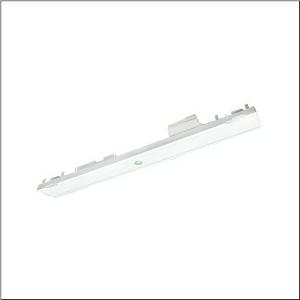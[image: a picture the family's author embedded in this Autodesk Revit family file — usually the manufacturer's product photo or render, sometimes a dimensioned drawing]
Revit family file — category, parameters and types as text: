
# Revit family: licross_56tl117c4x31
name_source: partatom
category: Lighting Fixtures
units: mm (PartAtom-declared; Revit-internal decimal feet)

## family parameters
Cut with Voids When Loaded = No
Host = Face
Light Source = No
Part Type = Normal
Room Calculation Point = No
Round Connector Dimension = Use Diameter
Shared = No

## types (1)
- Licross (1 x LED, 310 lm, 3.9 W, 4000K)
    Apparent Load = 4 VA
    CIE Flux Codes = 84 95 98 100 100
    Color Rendering = 70
    Color Temperature = 4000K
    Default Elevation = 1800 mm
    Description = Licross, luminaire insert, of sheet steel, coil coated, white, length: 500mm, width: 59mm, height: 60mm, mounting height: 7..17m, emergency light element,LED rated luminous flux: 310lm, light colour: 740, control gear: CEAG, with plug, 6-pole, with phase selection, mains connection: 220..240V, AC/DC, 0/50..60Hz, rated input power: 3.9W, internal wiring halogen-free, for trunking rail, 9..14-core, for emergency light function, supply monitoring module CEAG, with address switch, choice between two emergency light lines via tool-free moving of contact pin prior to installation in trunking rail, primary light control with lens, of PMMA, primary optical cover: cover, of PMMA, light emission: direct distribution, primary light characteristic: symmetric,  for area, compatible with all CEAG STAR technology systems (ZB-S, DG-S (DualGuard-S), LP-STAR, AT-S+), protection rating (complete): IP40, insulation class (complete): insulation class I (protective earthing), certification: CE, UKCA, protection symbol: D if used in an environment without relevant dust loads, impact resistance: IK06, permissible ambient temperature for indoor applications: -20..+40°C, packaging unit: 1 piece
    Height = 60 mm  [stored 0.19685 ft]
    Lamp = 1 x LED
    Lamp Light Flux = 310 lm
    Lamp Power = 3.9 W
    Lamp count = 1
    Length = 500 mm  [stored 1.64042 ft]
    Luminous efficacy = 79 lm/W
    Manufacturer = Siteco
    ModVariant = No
    Model = 56TL117C4X31
    Mounting Place = Ceiling
    Mounting Type = Pendant
    Number of Poles = 1
    OnlyDefault = Yes
    Power Factor = 1
    Product Name = Licross
    Product group = luminaire insert | ceiling pendant
    ProductGroupID = 901
    Protection Class = Protection class I
    Protection Degree = IP 40
    RLX_Detail_Level = 1
    RLX_Emergency_Light_Flux = 0 lm
    RLX_Emergency_Type = 0
    RLX_Emergency_Type_DB = No
    RlxData = <blob elided: 17845 chars, md5=55b05414>
    Socket = socket
    Standby Power = 0 W
    System Light Flux = 310 lm
    System Power = 4 W
    Type Comments = Product without accessories
    Type Image = l_1251804.jpg
    URL = http://relux.com
    VarID = ---
    Voltage = 0 V
    Weight = 0.00 kg
    Width = 59 mm

note: [stored X ft] marks values corroborated as IEEE doubles in the binary element streams (Revit-internal decimal feet)

## geometry (parser evidence)
native form markers: Blend x4, Sweep x12
no freeform markers — native parametric forms only
